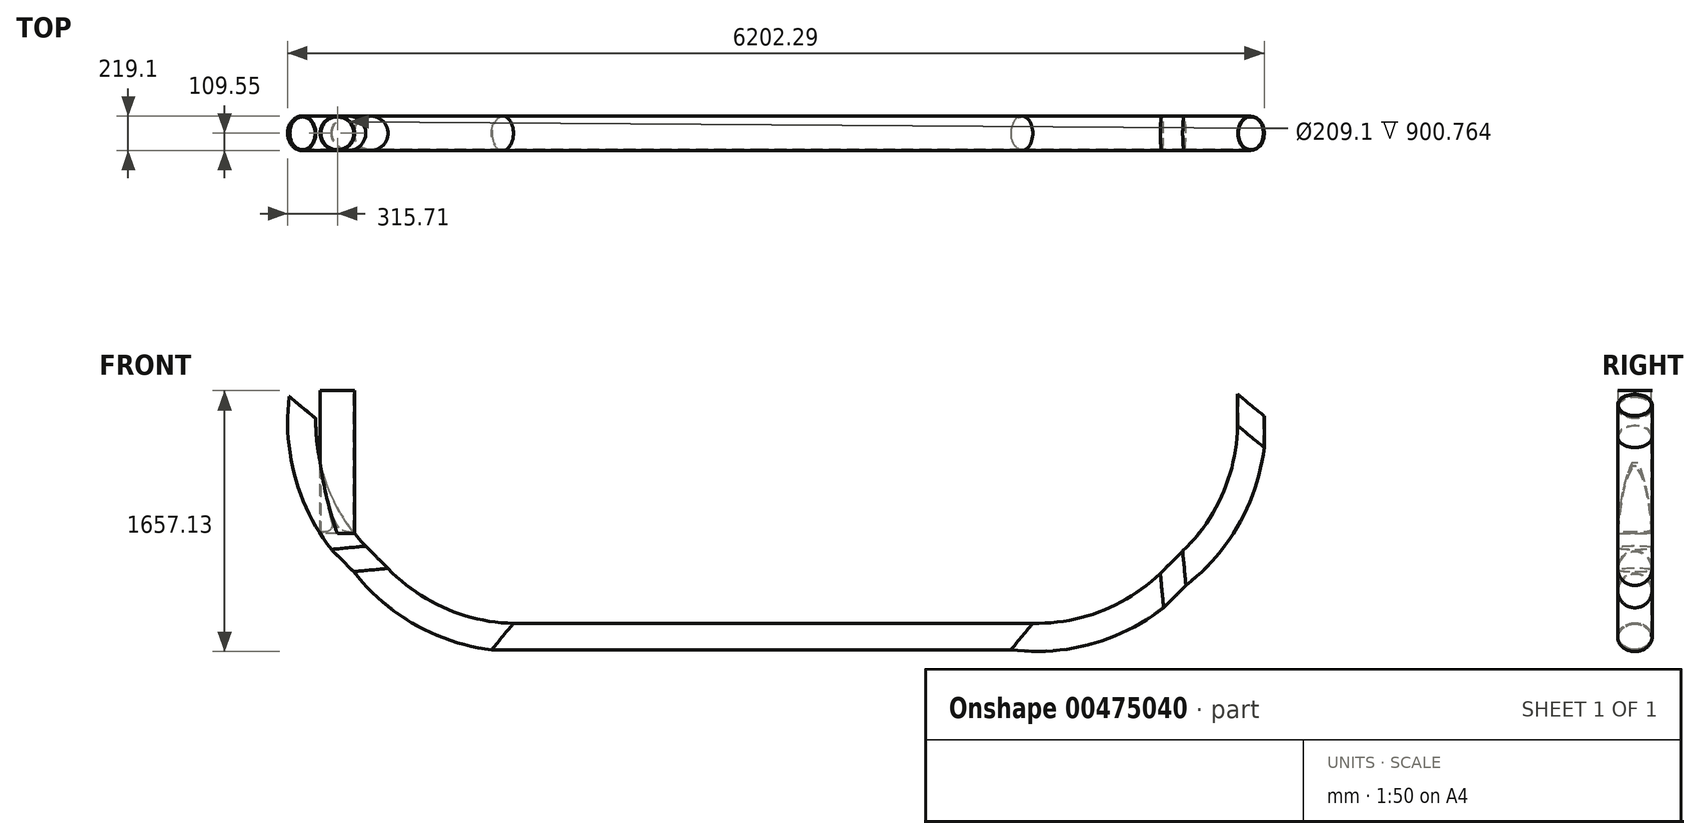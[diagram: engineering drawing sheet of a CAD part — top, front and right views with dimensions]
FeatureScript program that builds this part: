
annotation { "Feature Type Name" : "Feature", "Feature Type Description" : "" }
export const myFeature = defineFeature(function(context is Context, id is Id, definition is map)
    precondition{}
    {
        {
            var Q0;
            Q0=qCreatedBy(makeId("Front.planeOp"),FACE);
            var sketch = newSketch(context, id + "F0", { "sketchPlane" : qUnion([Q0])});
            skLineSegment(sketch, "E0", {"start": v(-1649.03, 0) * mm, "end": v(0, 0) * mm, "construction": true});
            skLineSegment(sketch, "E1", {"start": v(-2356.14, 292.9) * mm, "end": v(-2497.56, 434.31) * mm, "construction": true});
            skArc(sketch, "E2", {"start": v(-1649.03, 0) * mm, "mid": v(-2031.71, 76.12) * mm, "end": v(-2356.14, 292.9) * mm, "construction": true});
            skArc(sketch, "E3", {"start": v(-2497.56, 434.31) * mm, "mid": v(-2714.33, 758.74) * mm, "end": v(-2790.45, 1141.42) * mm, "construction": true});
            skPoint(sketch, "E4", {"position": v(0, 0) * mm});
            skArc(sketch, "E5.3", {"start": v(-2575.02, 356.85) * mm, "mid": v(-2815.54, 716.81) * mm, "end": v(-2900, 1141.42) * mm});
            skArc(sketch, "E5.5", {"start": v(-1649.03, -109.55) * mm, "mid": v(-2073.64, -25.1) * mm, "end": v(-2433.6, 215.43) * mm});
            skLineSegment(sketch, "E5.6", {"start": v(-1649.03, -109.55) * mm, "end": v(0, -109.55) * mm});
            skLineSegment(sketch, "E6", {"start": v(-1649.03, 0) * mm, "end": v(-1649.03, -109.55) * mm});
            skLineSegment(sketch, "E7", {"start": v(-2900, 1141.42) * mm, "end": v(-2790.45, 1141.42) * mm});
            skLineSegment(sketch, "E8", {"start": v(0, 0) * mm, "end": v(0, -109.55) * mm, "construction": true});
            skLineSegment(sketch, "E9", {"start": v(-2575.02, 356.85) * mm, "end": v(-2433.6, 215.43) * mm});
            skLineSegment(sketch, "E10.MirrorCS", {"start": v(2356.14, 292.9) * mm, "end": v(2497.56, 434.31) * mm, "construction": true});
            skLineSegment(sketch, "E11.MirrorCS", {"start": v(2497.56, 434.31) * mm, "end": v(2575.02, 356.85) * mm});
            skLineSegment(sketch, "E12.MirrorCS", {"start": v(2356.14, 292.9) * mm, "end": v(2433.6, 215.43) * mm});
            skLineSegment(sketch, "E13.MirrorCS", {"start": v(2575.02, 356.85) * mm, "end": v(2433.6, 215.43) * mm});
            skLineSegment(sketch, "E14.MirrorCS", {"start": v(1649.03, 0) * mm, "end": v(1649.03, -109.55) * mm});
            skLineSegment(sketch, "E15.MirrorCS", {"start": v(2900, 1141.42) * mm, "end": v(2790.45, 1141.42) * mm});
            skArc(sketch, "E16.MirrorCS", {"start": v(1649.03, -109.55) * mm, "mid": v(2073.64, -25.1) * mm, "end": v(2433.6, 215.43) * mm});
            skArc(sketch, "E17.MirrorCS", {"start": v(1649.03, 0) * mm, "mid": v(2031.71, 76.12) * mm, "end": v(2356.14, 292.9) * mm, "construction": true});
            skArc(sketch, "E18.MirrorCS", {"start": v(2575.02, 356.85) * mm, "mid": v(2815.54, 716.81) * mm, "end": v(2900, 1141.42) * mm});
            skLineSegment(sketch, "E19.MirrorCS", {"start": v(1649.03, 0) * mm, "end": v(0, 0) * mm, "construction": true});
            skLineSegment(sketch, "E20.MirrorCS", {"start": v(1649.03, -109.55) * mm, "end": v(0, -109.55) * mm});
            skArc(sketch, "E21.MirrorCS", {"start": v(2497.56, 434.31) * mm, "mid": v(2714.33, 758.74) * mm, "end": v(2790.45, 1141.42) * mm, "construction": true});
            skLineSegment(sketch, "E22", {"start": v(-2790.45, 1141.42) * mm, "end": v(-2790.45, 1341.42) * mm, "construction": true});
            skLineSegment(sketch, "E23", {"start": v(-2790.45, 1341.42) * mm, "end": v(-2900, 1341.42) * mm});
            skLineSegment(sketch, "E24", {"start": v(-2900, 1341.42) * mm, "end": v(-2900, 1141.42) * mm});
            skLineSegment(sketch, "E25.MirrorCS", {"start": v(2790.45, 1341.42) * mm, "end": v(2900, 1341.42) * mm});
            skLineSegment(sketch, "E26.MirrorCS", {"start": v(2790.45, 1141.42) * mm, "end": v(2790.45, 1341.42) * mm, "construction": true});
            skLineSegment(sketch, "E27.MirrorCS", {"start": v(2900, 1341.42) * mm, "end": v(2900, 1141.42) * mm});
            skLineSegment(sketch, "E28", {"start": v(-2575.02, 356.85) * mm, "end": v(-2497.56, 434.31) * mm});
            skLineSegment(sketch, "E29", {"start": v(-2433.6, 215.43) * mm, "end": v(-2356.14, 292.9) * mm});
            skLineSegment(sketch, "E30.bottom", {"start": v(2600, -159.55) * mm, "end": v(-2600, -159.55) * mm});
            skLineSegment(sketch, "E30.top", {"start": v(3000, 540.45) * mm, "end": v(-3000, 540.45) * mm});
            skLineSegment(sketch, "E30.left", {"start": v(3000, 340.45) * mm, "end": v(3000, 540.45) * mm});
            skLineSegment(sketch, "E30.right", {"start": v(-3000, 340.45) * mm, "end": v(-3000, 540.45) * mm});
            skLineSegment(sketch, "E31", {"start": v(-3000, 340.45) * mm, "end": v(-2600, -159.55) * mm});
            skLineSegment(sketch, "E32", {"start": v(2600, -159.55) * mm, "end": v(3000, 340.45) * mm});
            skPoint(sketch, "E33", {"position": v(0, -159.55) * mm});
            skLineSegment(sketch, "E34", {"start": v(-2723.58, 541.12) * mm, "end": v(-3000, 541.12) * mm});
            skSolve(sketch);
        }
        {
            var Q0;
            Q0=qCreatedBy(makeId("Top.planeOp"),FACE);
            cPlane(context, id + "F1", {"entities" : qUnion([Q0]), "cplaneType" : CPlaneType.OFFSET, "offset" : 1341.42 * mm, "width" : 150 * mm, "height" : 150 * mm});
        }
        {
            var Q0;
            Q0=qCreatedBy(id+"F1.planeOp",FACE);
            var sketch = newSketch(context, id + "F2", { "sketchPlane" : qUnion([Q0])});
            skCircle(sketch, "E35", {"center": v(-2790.45, 0) * mm, "radius": 109.55 * mm});
            skCircle(sketch, "E36", {"center": v(-2790.45, 0) * mm, "radius": 104.55 * mm});
            skSolve(sketch);
        }
        {
            var Q0;
            Q0=makeQuery(id+"F2.imprint","IMPRINT",FACE,{"disambiguationData":[TD([[makeQuery(id+"F2.imprint","IMPRINT",EDGE,{"derivedFrom":sQuery(id+"F2.wireOp",EDGE,"E35")}),1.0]])]});
            var Q1;
            Q1=sQuery(id+"F0.wireOp",VERTEX,"E3.end");
            extrude(context, id + "F3", {"entities" : qUnion([Q0]), "endBound" : BoundingType.UP_TO_VERTEX, "oppositeDirection" : true, "endBoundEntityVertex" : qUnion([Q1]), "depth" : 91 * mm});
        }
        {
            var Q0;
            Q0=makeQuery(id+"F3.opExtrude","CAP_FACE",FACE,{"disambiguationData":[OSD([sQuery(id+"F2.wireOp",EDGE,"E35"),sQuery(id+"F2.wireOp",EDGE,"E36")])],"isStart":false});
            var Q1;
            Q1=sQuery(id+"F0.wireOp",EDGE,"E5.3");
            var Q2;
            Q2=sQuery(id+"F0.wireOp",EDGE,"E9");
            var Q3;
            Q3=sQuery(id+"F0.wireOp",EDGE,"E5.5");
            var Q4;
            Q4=sQuery(id+"F0.wireOp",EDGE,"E5.6");
            var Q5;
            Q5=sQuery(id+"F0.wireOp",EDGE,"E20.MirrorCS");
            var Q6;
            Q6=sQuery(id+"F0.wireOp",EDGE,"E16.MirrorCS");
            var Q7;
            Q7=sQuery(id+"F0.wireOp",EDGE,"E13.MirrorCS");
            var Q8;
            Q8=sQuery(id+"F0.wireOp",EDGE,"E18.MirrorCS");
            var Q9;
            Q9=sQuery(id+"F0.wireOp",EDGE,"E27.MirrorCS");
            sweep(context, id + "F4", {"operationType" : NewBodyOperationType.ADD, "profiles" : qUnion([Q0]), "path" : qUnion([Q1, Q2, Q3, Q4, Q5, Q6, Q7, Q8, Q9])});
        }
    });
